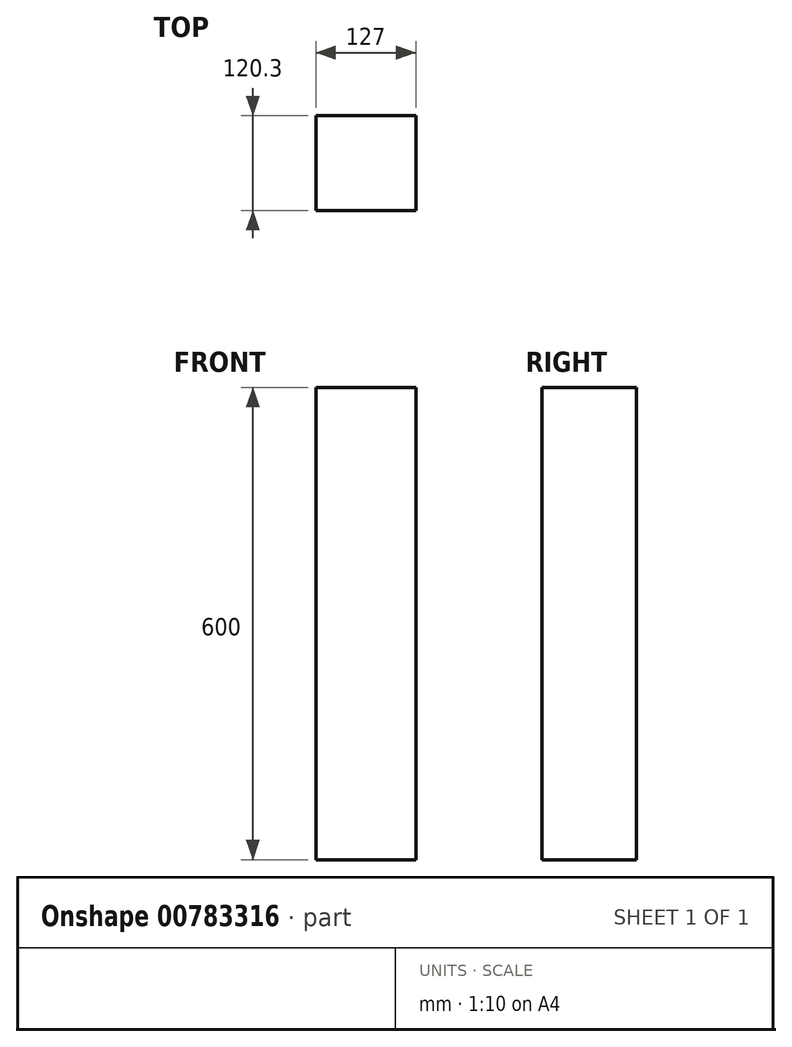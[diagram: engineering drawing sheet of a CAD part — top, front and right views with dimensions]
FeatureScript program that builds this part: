
annotation { "Feature Type Name" : "Feature", "Feature Type Description" : "" }
export const myFeature = defineFeature(function(context is Context, id is Id, definition is map)
    precondition{}
    {
        {
            var Q0;
            Q0=qCreatedBy(makeId("Top.planeOp"),FACE);
            var sketch = newSketch(context, id + "F0", { "sketchPlane" : qUnion([Q0])});
            skLineSegment(sketch, "E0.bottom", {"start": v(63.5, 60.15) * mm, "end": v(-63.5, 60.15) * mm});
            skLineSegment(sketch, "E0.top", {"start": v(63.5, -60.15) * mm, "end": v(-63.5, -60.15) * mm});
            skLineSegment(sketch, "E0.left", {"start": v(63.5, 60.15) * mm, "end": v(63.5, -60.15) * mm});
            skLineSegment(sketch, "E0.right", {"start": v(-63.5, 60.15) * mm, "end": v(-63.5, -60.15) * mm});
            skPoint(sketch, "E0.middle", {"position": v(0, 0) * mm});
            skSolve(sketch);
        }
        {
            var Q0;
            Q0=makeQuery(id+"F0.imprint","IMPRINT",FACE,{"disambiguationData":[TD([[makeQuery(id+"F0.imprint","IMPRINT",EDGE,{"derivedFrom":sQuery(id+"F0.wireOp",EDGE,"E0.bottom")}),1.0]])]});
            extrude(context, id + "F1", {"entities" : qUnion([Q0]), "depth" : 600 * mm, "offsetDistance" : 25.4 * mm});
        }
    });
